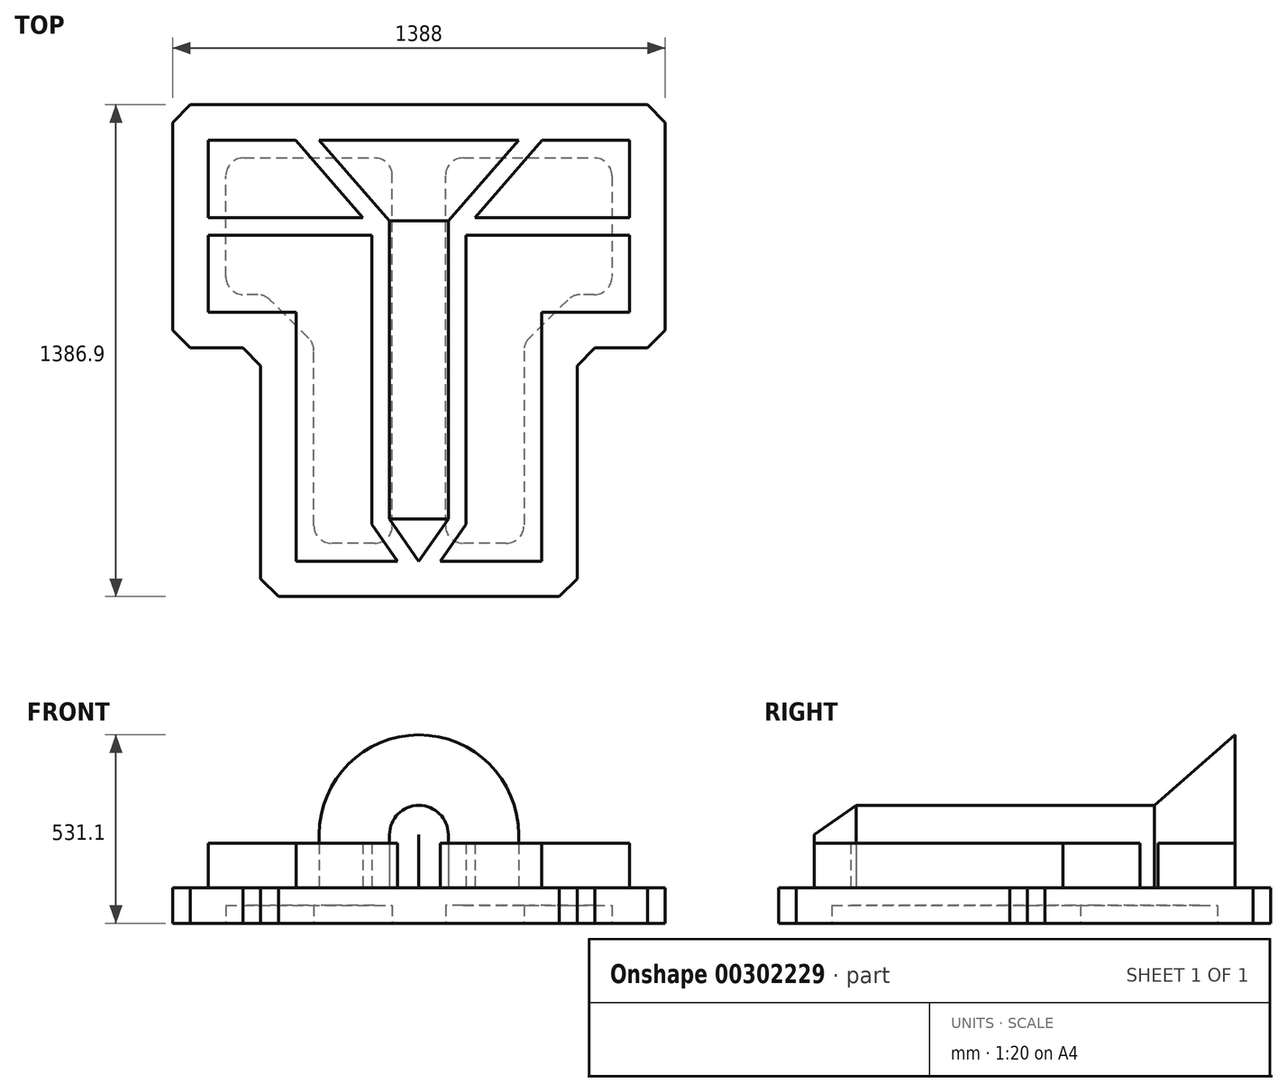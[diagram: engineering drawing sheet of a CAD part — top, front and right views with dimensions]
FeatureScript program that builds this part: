
annotation { "Feature Type Name" : "Feature", "Feature Type Description" : "" }
export const myFeature = defineFeature(function(context is Context, id is Id, definition is map)
    precondition{}
    {
        {
            var Q0;
            Q0=qCreatedBy(makeId("Top.planeOp"),FACE);
            var sketch = newSketch(context, id + "F0", { "sketchPlane" : qUnion([Q0])});
            skLineSegment(sketch, "E0", {"start": v(0, 0) * mm, "end": v(-281.1, 0) * mm});
            skLineSegment(sketch, "E1", {"start": v(-281.1, 0) * mm, "end": v(-82.6, -227.7) * mm});
            skLineSegment(sketch, "E2", {"start": v(-82.6, -227.7) * mm, "end": v(-82.6, -1068) * mm});
            skLineSegment(sketch, "E3", {"start": v(-82.6, -1068) * mm, "end": v(0, -1186.9) * mm});
            skLineSegment(sketch, "E4", {"start": v(0, -1186.9) * mm, "end": v(0, 0) * mm});
            skLineSegment(sketch, "E5", {"start": v(-594, 0) * mm, "end": v(-594, -217.8) * mm});
            skLineSegment(sketch, "E6", {"start": v(-594, -217.8) * mm, "end": v(-157.56, -217.8) * mm});
            skLineSegment(sketch, "E7", {"start": v(-157.56, -217.8) * mm, "end": v(-347.43, 0) * mm});
            skLineSegment(sketch, "E8", {"start": v(-347.43, 0) * mm, "end": v(-594, 0) * mm});
            skLineSegment(sketch, "E9", {"start": v(-594, -267.8) * mm, "end": v(-132.6, -267.8) * mm});
            skLineSegment(sketch, "E10", {"start": v(-132.6, -267.8) * mm, "end": v(-132.6, -1083.66) * mm});
            skLineSegment(sketch, "E11", {"start": v(-132.6, -1083.66) * mm, "end": v(-60.88, -1186.9) * mm});
            skLineSegment(sketch, "E12", {"start": v(-60.88, -1186.9) * mm, "end": v(-346, -1186.9) * mm});
            skLineSegment(sketch, "E13", {"start": v(-346, -1186.9) * mm, "end": v(-346, -485.6) * mm});
            skLineSegment(sketch, "E14", {"start": v(-346, -485.6) * mm, "end": v(-594, -485.6) * mm});
            skLineSegment(sketch, "E15", {"start": v(-594, -485.6) * mm, "end": v(-594, -267.8) * mm});
            skLineSegment(sketch, "E16.MirrorCS", {"start": v(157.56, -217.8) * mm, "end": v(347.43, 0) * mm});
            skLineSegment(sketch, "E17.MirrorCS", {"start": v(347.43, 0) * mm, "end": v(594, 0) * mm});
            skLineSegment(sketch, "E18.MirrorCS", {"start": v(594, 0) * mm, "end": v(594, -217.8) * mm});
            skLineSegment(sketch, "E19.MirrorCS", {"start": v(594, -217.8) * mm, "end": v(157.56, -217.8) * mm});
            skLineSegment(sketch, "E20.MirrorCS", {"start": v(594, -267.8) * mm, "end": v(132.6, -267.8) * mm});
            skLineSegment(sketch, "E21.MirrorCS", {"start": v(594, -485.6) * mm, "end": v(594, -267.8) * mm});
            skLineSegment(sketch, "E22.MirrorCS", {"start": v(346, -485.6) * mm, "end": v(594, -485.6) * mm});
            skLineSegment(sketch, "E23.MirrorCS", {"start": v(346, -1186.9) * mm, "end": v(346, -485.6) * mm});
            skLineSegment(sketch, "E24.MirrorCS", {"start": v(60.88, -1186.9) * mm, "end": v(346, -1186.9) * mm});
            skLineSegment(sketch, "E25.MirrorCS", {"start": v(132.6, -1083.66) * mm, "end": v(60.88, -1186.9) * mm});
            skLineSegment(sketch, "E26.MirrorCS", {"start": v(132.6, -267.8) * mm, "end": v(132.6, -1083.66) * mm});
            skLineSegment(sketch, "E27.MirrorCS", {"start": v(0, 0) * mm, "end": v(281.1, 0) * mm});
            skLineSegment(sketch, "E28.MirrorCS", {"start": v(281.1, 0) * mm, "end": v(82.6, -227.7) * mm});
            skLineSegment(sketch, "E29.MirrorCS", {"start": v(82.6, -227.7) * mm, "end": v(82.6, -1068) * mm});
            skLineSegment(sketch, "E30.MirrorCS", {"start": v(82.6, -1068) * mm, "end": v(0, -1186.9) * mm});
            skLineSegment(sketch, "E31", {"start": v(0, 100) * mm, "end": v(-694, 100) * mm});
            skLineSegment(sketch, "E32", {"start": v(-694, 100) * mm, "end": v(-694, -585.6) * mm});
            skLineSegment(sketch, "E33", {"start": v(-694, -585.6) * mm, "end": v(-446, -585.6) * mm});
            skLineSegment(sketch, "E34", {"start": v(-446, -585.6) * mm, "end": v(-446, -1286.9) * mm});
            skLineSegment(sketch, "E35", {"start": v(-446, -1286.9) * mm, "end": v(0, -1286.9) * mm});
            skLineSegment(sketch, "E36.MirrorCS", {"start": v(0, 100) * mm, "end": v(694, 100) * mm});
            skLineSegment(sketch, "E37.MirrorCS", {"start": v(694, 100) * mm, "end": v(694, -585.6) * mm});
            skLineSegment(sketch, "E38.MirrorCS", {"start": v(694, -585.6) * mm, "end": v(446, -585.6) * mm});
            skLineSegment(sketch, "E39.MirrorCS", {"start": v(446, -1286.9) * mm, "end": v(0, -1286.9) * mm});
            skLineSegment(sketch, "E40.MirrorCS", {"start": v(446, -585.6) * mm, "end": v(446, -1286.9) * mm});
            skSolve(sketch);
        }
        {
            var Q0;
            Q0=makeQuery(id+"F0.imprint","IMPRINT",FACE,{"disambiguationData":[TD([[makeQuery(id+"F0.imprint","IMPRINT",EDGE,{"derivedFrom":sQuery(id+"F0.wireOp",EDGE,"E0")}),-1.0]])]});
            var Q1;
            Q1=makeQuery(id+"F0.imprint","IMPRINT",FACE,{"disambiguationData":[TD([[makeQuery(id+"F0.imprint","IMPRINT",EDGE,{"derivedFrom":sQuery(id+"F0.wireOp",EDGE,"E5")}),1.0]])]});
            var Q2;
            Q2=makeQuery(id+"F0.imprint","IMPRINT",FACE,{"disambiguationData":[TD([[makeQuery(id+"F0.imprint","IMPRINT",EDGE,{"derivedFrom":sQuery(id+"F0.wireOp",EDGE,"E9")}),-1.0]])]});
            var Q3;
            Q3=makeQuery(id+"F0.imprint","IMPRINT",FACE,{"disambiguationData":[TD([[makeQuery(id+"F0.imprint","IMPRINT",EDGE,{"derivedFrom":sQuery(id+"F0.wireOp",EDGE,"E4")}),-1.0]])]});
            var Q4;
            Q4=makeQuery(id+"F0.imprint","IMPRINT",FACE,{"disambiguationData":[TD([[makeQuery(id+"F0.imprint","IMPRINT",EDGE,{"derivedFrom":sQuery(id+"F0.wireOp",EDGE,"E20.MirrorCS")}),1.0]])]});
            var Q5;
            Q5=makeQuery(id+"F0.imprint","IMPRINT",FACE,{"disambiguationData":[TD([[makeQuery(id+"F0.imprint","IMPRINT",EDGE,{"derivedFrom":sQuery(id+"F0.wireOp",EDGE,"E16.MirrorCS")}),-1.0]])]});
            var Q6;
            Q6=makeQuery(id+"F0.imprint","IMPRINT",FACE,{"disambiguationData":[TD([[makeQuery(id+"F0.imprint","IMPRINT",EDGE,{"derivedFrom":sQuery(id+"F0.wireOp",EDGE,"E0")}),1.0]])]});
            extrude(context, id + "F1", {"entities" : qUnion([Q0, Q1, Q2, Q3, Q4, Q5, Q6]), "oppositeDirection" : true, "depth" : 100 * mm});
        }
        {
            var Q0;
            Q0=makeQuery(id+"F0.imprint","IMPRINT",FACE,{"disambiguationData":[TD([[makeQuery(id+"F0.imprint","IMPRINT",EDGE,{"derivedFrom":sQuery(id+"F0.wireOp",EDGE,"E5")}),1.0]])]});
            var Q1;
            Q1=makeQuery(id+"F0.imprint","IMPRINT",FACE,{"disambiguationData":[TD([[makeQuery(id+"F0.imprint","IMPRINT",EDGE,{"derivedFrom":sQuery(id+"F0.wireOp",EDGE,"E9")}),-1.0]])]});
            var Q2;
            Q2=makeQuery(id+"F0.imprint","IMPRINT",FACE,{"disambiguationData":[TD([[makeQuery(id+"F0.imprint","IMPRINT",EDGE,{"derivedFrom":sQuery(id+"F0.wireOp",EDGE,"E20.MirrorCS")}),1.0]])]});
            var Q3;
            Q3=makeQuery(id+"F0.imprint","IMPRINT",FACE,{"disambiguationData":[TD([[makeQuery(id+"F0.imprint","IMPRINT",EDGE,{"derivedFrom":sQuery(id+"F0.wireOp",EDGE,"E16.MirrorCS")}),-1.0]])]});
            extrude(context, id + "F2", {"entities" : qUnion([Q0, Q1, Q2, Q3]), "operationType" : NewBodyOperationType.ADD, "depth" : 125 * mm});
        }
        {
            var Q0;
            Q0=makeQuery(id+"F0.imprint","IMPRINT",FACE,{"disambiguationData":[TD([[makeQuery(id+"F0.imprint","IMPRINT",EDGE,{"derivedFrom":sQuery(id+"F0.wireOp",EDGE,"E0")}),1.0]])]});
            var Q1;
            Q1=makeQuery(id+"F0.imprint","IMPRINT",FACE,{"disambiguationData":[TD([[makeQuery(id+"F0.imprint","IMPRINT",EDGE,{"derivedFrom":sQuery(id+"F0.wireOp",EDGE,"E4")}),-1.0]])]});
            extrude(context, id + "F3", {"entities" : qUnion([Q0, Q1]), "operationType" : NewBodyOperationType.ADD, "depth" : 150 * mm});
        }
        {
            var Q0;
            Q0=makeQuery(id+"F3.opExtrude","CAP_FACE",FACE,{"disambiguationData":[OSD([sQuery(id+"F0.wireOp",EDGE,"E0"),sQuery(id+"F0.wireOp",EDGE,"E1"),sQuery(id+"F0.wireOp",EDGE,"E2"),sQuery(id+"F0.wireOp",EDGE,"E3"),sQuery(id+"F0.wireOp",EDGE,"E27.MirrorCS"),sQuery(id+"F0.wireOp",EDGE,"E28.MirrorCS"),sQuery(id+"F0.wireOp",EDGE,"E29.MirrorCS"),sQuery(id+"F0.wireOp",EDGE,"E30.MirrorCS")])],"isStart":false});
            var sketch = newSketch(context, id + "F4", { "sketchPlane" : qUnion([Q0])});
            skLineSegment(sketch, "E41", {"start": v(0, 0) * mm, "end": v(0, -1186.9) * mm});
            skSolve(sketch);
        }
        {
            var Q0;
            {var subQ1=sQuery(id+"F4.wireOp",EDGE,"E41");Q0=makeQuery(id+"F4.imprint","IMPRINT",FACE,{"disambiguationData":[TD([[makeQuery(id+"F4.imprint","IMPRINT",EDGE,{"derivedFrom":subQ1}),-1.0]])]});}
            var Q1;
            Q1=sQuery(id+"F4.wireOp",EDGE,"E41");
            revolve(context, id + "F5", {"operationType" : NewBodyOperationType.ADD, "entities" : qUnion([Q0]), "axis" : qUnion([Q1]), "revolveType" : RevolveType.ONE_DIRECTION, "oppositeDirection" : true, "angle" : 180 * degree});
        }
        {
            var Q0;
            Q0=makeQuery(id+"F1.opExtrude","SWEPT_EDGE",EDGE,{"disambiguationData":[OSD([sQuery(id+"F0.wireOp",EDGE,"E31"),sQuery(id+"F0.wireOp",EDGE,"E32")])]});
            var Q1;
            Q1=makeQuery(id+"F1.opExtrude","SWEPT_EDGE",EDGE,{"disambiguationData":[OSD([sQuery(id+"F0.wireOp",EDGE,"E32"),sQuery(id+"F0.wireOp",EDGE,"E33")])]});
            var Q2;
            Q2=makeQuery(id+"F1.opExtrude","SWEPT_EDGE",EDGE,{"disambiguationData":[OSD([sQuery(id+"F0.wireOp",EDGE,"E34"),sQuery(id+"F0.wireOp",EDGE,"E35")])]});
            var Q3;
            Q3=makeQuery(id+"F1.opExtrude","SWEPT_EDGE",EDGE,{"disambiguationData":[OSD([sQuery(id+"F0.wireOp",EDGE,"E39.MirrorCS"),sQuery(id+"F0.wireOp",EDGE,"E40.MirrorCS")])]});
            var Q4;
            Q4=makeQuery(id+"F1.opExtrude","SWEPT_EDGE",EDGE,{"disambiguationData":[OSD([sQuery(id+"F0.wireOp",EDGE,"E33"),sQuery(id+"F0.wireOp",EDGE,"E34")])]});
            var Q5;
            Q5=makeQuery(id+"F1.opExtrude","SWEPT_EDGE",EDGE,{"disambiguationData":[OSD([sQuery(id+"F0.wireOp",EDGE,"E38.MirrorCS"),sQuery(id+"F0.wireOp",EDGE,"E40.MirrorCS")])]});
            var Q6;
            Q6=makeQuery(id+"F1.opExtrude","SWEPT_EDGE",EDGE,{"disambiguationData":[OSD([sQuery(id+"F0.wireOp",EDGE,"E37.MirrorCS"),sQuery(id+"F0.wireOp",EDGE,"E38.MirrorCS")])]});
            var Q7;
            Q7=makeQuery(id+"F1.opExtrude","SWEPT_EDGE",EDGE,{"disambiguationData":[OSD([sQuery(id+"F0.wireOp",EDGE,"E36.MirrorCS"),sQuery(id+"F0.wireOp",EDGE,"E37.MirrorCS")])]});
            chamfer(context, id + "F6", {"entities" : qUnion([Q0, Q1, Q2, Q3, Q4, Q5, Q6, Q7]), "width" : 50 * mm, "tangentPropagation" : true});
        }
        {
            var Q0;
            Q0=makeQuery(id+"F1.opExtrude","CAP_FACE",FACE,{"disambiguationData":[OSD([sQuery(id+"F0.wireOp",EDGE,"E31"),sQuery(id+"F0.wireOp",EDGE,"E32"),sQuery(id+"F0.wireOp",EDGE,"E33"),sQuery(id+"F0.wireOp",EDGE,"E34"),sQuery(id+"F0.wireOp",EDGE,"E35"),sQuery(id+"F0.wireOp",EDGE,"E36.MirrorCS"),sQuery(id+"F0.wireOp",EDGE,"E37.MirrorCS"),sQuery(id+"F0.wireOp",EDGE,"E38.MirrorCS"),sQuery(id+"F0.wireOp",EDGE,"E39.MirrorCS"),sQuery(id+"F0.wireOp",EDGE,"E40.MirrorCS")])],"isStart":false});
            var sketch = newSketch(context, id + "F7", { "sketchPlane" : qUnion([Q0])});
            skLineSegment(sketch, "E42.0", {"start": v(-544, 435.6) * mm, "end": v(-544, 50) * mm});
            skLineSegment(sketch, "E42.1", {"start": v(-433.87, 435.6) * mm, "end": v(-544, 435.6) * mm});
            skLineSegment(sketch, "E42.2", {"start": v(-544, 50) * mm, "end": v(544, 50) * mm});
            skLineSegment(sketch, "E42.3", {"start": v(-296, 573.47) * mm, "end": v(-433.87, 435.6) * mm});
            skLineSegment(sketch, "E42.4", {"start": v(-296, 1136.9) * mm, "end": v(-296, 573.47) * mm});
            skLineSegment(sketch, "E42.5", {"start": v(296, 1136.9) * mm, "end": v(-296, 1136.9) * mm});
            skLineSegment(sketch, "E42.6", {"start": v(544, 50) * mm, "end": v(544, 435.6) * mm});
            skLineSegment(sketch, "E42.7", {"start": v(544, 435.6) * mm, "end": v(433.87, 435.6) * mm});
            skLineSegment(sketch, "E42.8", {"start": v(433.87, 435.6) * mm, "end": v(296, 573.47) * mm});
            skLineSegment(sketch, "E42.9", {"start": v(296, 573.47) * mm, "end": v(296, 1136.9) * mm});
            skLineSegment(sketch, "E43", {"start": v(0, 1136.9) * mm, "end": v(0, 50) * mm});
            skLineSegment(sketch, "E44", {"start": v(-75, 1136.9) * mm, "end": v(-75, 50) * mm});
            skLineSegment(sketch, "E45.MirrorCS", {"start": v(75, 1136.9) * mm, "end": v(75, 50) * mm});
            skSolve(sketch);
        }
        {
            var Q0;
            {var subQ1=sQuery(id+"F7.wireOp",EDGE,"E42.0");Q0=makeQuery(id+"F7.imprint","IMPRINT",FACE,{"disambiguationData":[TD([[makeQuery(id+"F7.imprint","IMPRINT",EDGE,{"derivedFrom":subQ1}),1.0]])]});}
            var Q1;
            {var subQ0=sQuery(id+"F7.wireOp",EDGE,"E42.6");Q1=makeQuery(id+"F7.imprint","IMPRINT",FACE,{"disambiguationData":[TD([[makeQuery(id+"F7.imprint","IMPRINT",EDGE,{"derivedFrom":subQ0}),1.0]])]});}
            extrude(context, id + "F8", {"entities" : qUnion([Q0, Q1]), "operationType" : NewBodyOperationType.REMOVE, "oppositeDirection" : true, "depth" : 50 * mm});
        }
        {
            var Q0;
            Q0=makeQuery(id+"F8.boolean.opBoolean","COPY",EDGE,{"derivedFrom":makeQuery(id+"F8.opExtrude","SWEPT_EDGE",EDGE,{"disambiguationData":[OSD([sQuery(id+"F7.wireOp",EDGE,"E42.0"),sQuery(id+"F7.wireOp",EDGE,"E42.1")])]})});
            var Q1;
            Q1=makeQuery(id+"F8.boolean.opBoolean","COPY",EDGE,{"derivedFrom":makeQuery(id+"F8.opExtrude","SWEPT_EDGE",EDGE,{"disambiguationData":[OSD([sQuery(id+"F7.wireOp",EDGE,"E42.1"),sQuery(id+"F7.wireOp",EDGE,"E42.3")])]})});
            var Q2;
            Q2=makeQuery(id+"F8.boolean.opBoolean","COPY",EDGE,{"derivedFrom":makeQuery(id+"F8.opExtrude","SWEPT_EDGE",EDGE,{"disambiguationData":[OSD([sQuery(id+"F7.wireOp",EDGE,"E42.3"),sQuery(id+"F7.wireOp",EDGE,"E42.4")])]})});
            var Q3;
            Q3=makeQuery(id+"F8.boolean.opBoolean","COPY",EDGE,{"derivedFrom":makeQuery(id+"F8.opExtrude","SWEPT_EDGE",EDGE,{"disambiguationData":[OSD([sQuery(id+"F7.wireOp",EDGE,"E42.4"),sQuery(id+"F7.wireOp",EDGE,"E42.5")])]})});
            var Q4;
            Q4=makeQuery(id+"F8.boolean.opBoolean","COPY",EDGE,{"derivedFrom":makeQuery(id+"F8.opExtrude","SWEPT_EDGE",EDGE,{"disambiguationData":[OSD([sQuery(id+"F7.wireOp",EDGE,"E42.5"),sQuery(id+"F7.wireOp",EDGE,"E44")])]})});
            var Q5;
            Q5=makeQuery(id+"F8.boolean.opBoolean","COPY",EDGE,{"derivedFrom":makeQuery(id+"F8.opExtrude","SWEPT_EDGE",EDGE,{"disambiguationData":[OSD([sQuery(id+"F7.wireOp",EDGE,"E42.2"),sQuery(id+"F7.wireOp",EDGE,"E44")])]})});
            var Q6;
            Q6=makeQuery(id+"F8.boolean.opBoolean","COPY",EDGE,{"derivedFrom":makeQuery(id+"F8.opExtrude","SWEPT_EDGE",EDGE,{"disambiguationData":[OSD([sQuery(id+"F7.wireOp",EDGE,"E42.0"),sQuery(id+"F7.wireOp",EDGE,"E42.2")])]})});
            var Q7;
            Q7=makeQuery(id+"F8.boolean.opBoolean","COPY",EDGE,{"derivedFrom":makeQuery(id+"F8.opExtrude","SWEPT_EDGE",EDGE,{"disambiguationData":[OSD([sQuery(id+"F7.wireOp",EDGE,"E42.2"),sQuery(id+"F7.wireOp",EDGE,"E45.MirrorCS")])]})});
            var Q8;
            Q8=makeQuery(id+"F8.boolean.opBoolean","COPY",EDGE,{"derivedFrom":makeQuery(id+"F8.opExtrude","SWEPT_EDGE",EDGE,{"disambiguationData":[OSD([sQuery(id+"F7.wireOp",EDGE,"E42.2"),sQuery(id+"F7.wireOp",EDGE,"E42.6")])]})});
            var Q9;
            Q9=makeQuery(id+"F8.boolean.opBoolean","COPY",EDGE,{"derivedFrom":makeQuery(id+"F8.opExtrude","SWEPT_EDGE",EDGE,{"disambiguationData":[OSD([sQuery(id+"F7.wireOp",EDGE,"E42.6"),sQuery(id+"F7.wireOp",EDGE,"E42.7")])]})});
            var Q10;
            Q10=makeQuery(id+"F8.boolean.opBoolean","COPY",EDGE,{"derivedFrom":makeQuery(id+"F8.opExtrude","SWEPT_EDGE",EDGE,{"disambiguationData":[OSD([sQuery(id+"F7.wireOp",EDGE,"E42.7"),sQuery(id+"F7.wireOp",EDGE,"E42.8")])]})});
            var Q11;
            Q11=makeQuery(id+"F8.boolean.opBoolean","COPY",EDGE,{"derivedFrom":makeQuery(id+"F8.opExtrude","SWEPT_EDGE",EDGE,{"disambiguationData":[OSD([sQuery(id+"F7.wireOp",EDGE,"E42.8"),sQuery(id+"F7.wireOp",EDGE,"E42.9")])]})});
            var Q12;
            Q12=makeQuery(id+"F8.boolean.opBoolean","COPY",EDGE,{"derivedFrom":makeQuery(id+"F8.opExtrude","SWEPT_EDGE",EDGE,{"disambiguationData":[OSD([sQuery(id+"F7.wireOp",EDGE,"E42.5"),sQuery(id+"F7.wireOp",EDGE,"E42.9")])]})});
            var Q13;
            Q13=makeQuery(id+"F8.boolean.opBoolean","COPY",EDGE,{"derivedFrom":makeQuery(id+"F8.opExtrude","SWEPT_EDGE",EDGE,{"disambiguationData":[OSD([sQuery(id+"F7.wireOp",EDGE,"E42.5"),sQuery(id+"F7.wireOp",EDGE,"E45.MirrorCS")])]})});
            fillet(context, id + "F9", {"entities" : qUnion([Q0, Q1, Q2, Q3, Q4, Q5, Q6, Q7, Q8, Q9, Q10, Q11, Q12, Q13]), "radius" : 50 * mm, "tangentPropagation" : true, "allowEdgeOverflow" : false});
        }
    });
